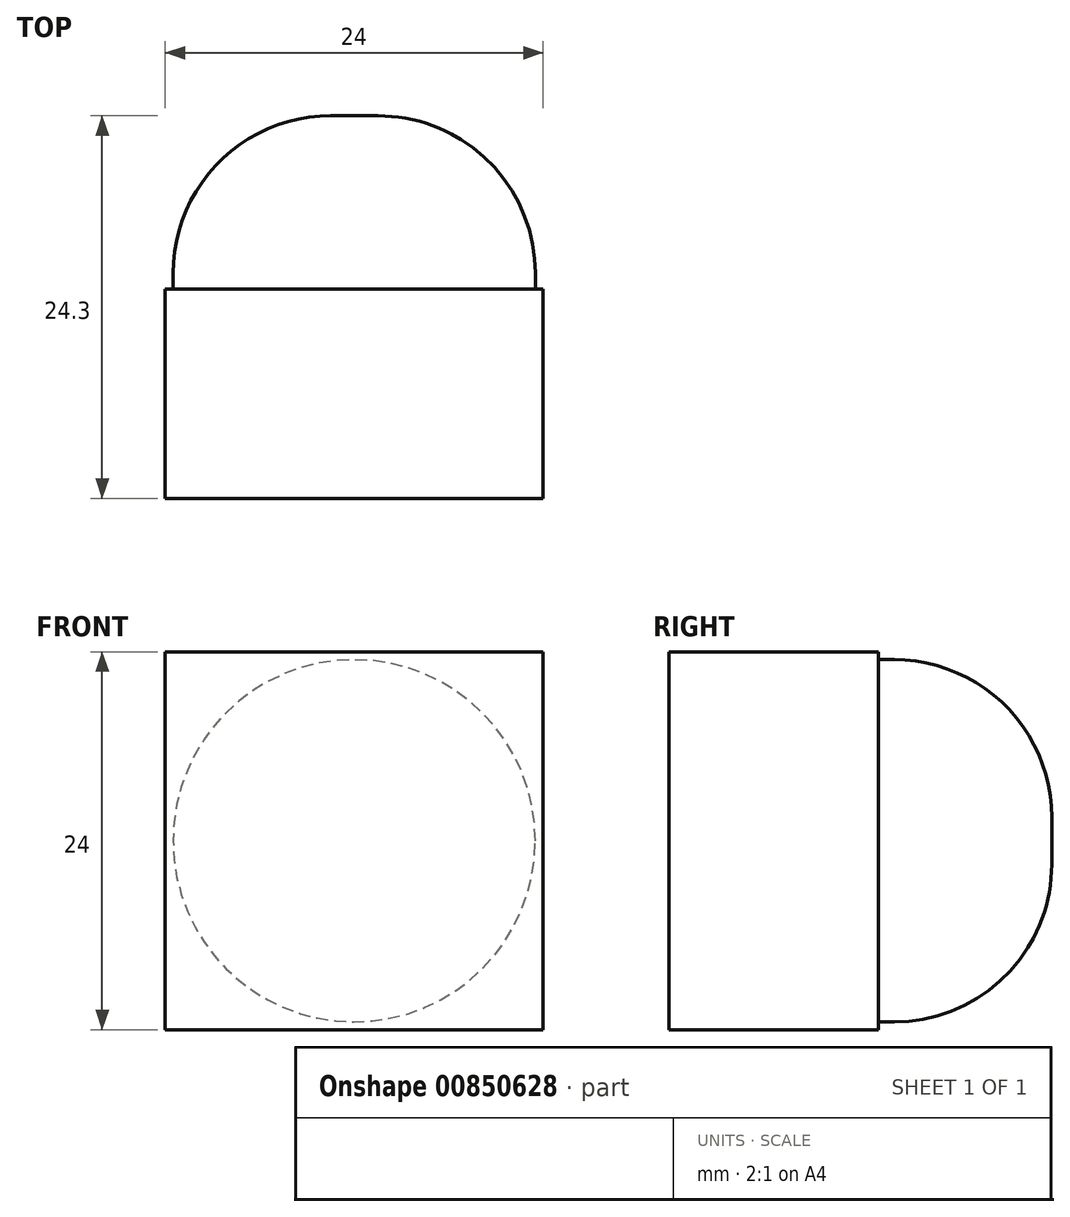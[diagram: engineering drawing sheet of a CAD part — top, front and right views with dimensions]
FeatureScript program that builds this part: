
annotation { "Feature Type Name" : "Feature", "Feature Type Description" : "" }
export const myFeature = defineFeature(function(context is Context, id is Id, definition is map)
    precondition{}
    {
        {
            var Q0;
            Q0=qCreatedBy(makeId("Front.planeOp"),FACE);
            var sketch = newSketch(context, id + "F0", { "sketchPlane" : qUnion([Q0])});
            skLineSegment(sketch, "E0.bottom", {"start": v(16.5, -12.5) * mm, "end": v(-16.5, -12.5) * mm});
            skLineSegment(sketch, "E0.top", {"start": v(16.5, 12.5) * mm, "end": v(-16.5, 12.5) * mm});
            skLineSegment(sketch, "E0.left", {"start": v(16.5, -12.5) * mm, "end": v(16.5, 12.5) * mm});
            skLineSegment(sketch, "E0.right", {"start": v(-16.5, -12.5) * mm, "end": v(-16.5, 12.5) * mm});
            skPoint(sketch, "E0.middle", {"position": v(0, 0) * mm});
            skLineSegment(sketch, "E1.bottom", {"start": v(-12, -12) * mm, "end": v(12, -12) * mm});
            skLineSegment(sketch, "E1.top", {"start": v(-12, 12) * mm, "end": v(12, 12) * mm});
            skLineSegment(sketch, "E1.left", {"start": v(-12, -12) * mm, "end": v(-12, 12) * mm});
            skLineSegment(sketch, "E1.right", {"start": v(12, -12) * mm, "end": v(12, 12) * mm});
            skLineSegment(sketch, "E2", {"start": v(16.5, 12.5) * mm, "end": v(14.2, 12.5) * mm});
            skLineSegment(sketch, "E3", {"start": v(14.2, 12.5) * mm, "end": v(14.2, 0) * mm});
            skCircle(sketch, "E4", {"center": v(14.2, 0) * mm, "radius": 0.75 * mm});
            skLineSegment(sketch, "E5.MirrorCS", {"start": v(-14.2, 12.5) * mm, "end": v(-14.2, 0) * mm});
            skCircle(sketch, "E6.MirrorC", {"center": v(-14.2, 0) * mm, "radius": 0.75 * mm});
            skSolve(sketch);
        }
        {
            var Q0;
            Q0 = qSketchRegion(id + "F0", true);
            var Q1;
            Q1=makeQuery(id+"F0.imprint","IMPRINT",FACE,{"disambiguationData":[TD([[makeQuery(id+"F0.imprint","IMPRINT",EDGE,{"derivedFrom":sQuery(id+"F0.wireOp",EDGE,"E1.bottom")}),1.0]])]});
            extrude(context, id + "F1", {"entities" : qUnion([Q0, Q1]), "depth" : 10 * mm, "offsetDistance" : 25 * mm});
        }
        {
            var Q0;
            Q0=makeQuery(id+"F0.imprint","IMPRINT",FACE,{"disambiguationData":[TD([[makeQuery(id+"F0.imprint","IMPRINT",EDGE,{"derivedFrom":sQuery(id+"F0.wireOp",EDGE,"E1.bottom")}),1.0]])]});
            extrude(context, id + "F2", {"entities" : qUnion([Q0]), "operationType" : NewBodyOperationType.ADD, "oppositeDirection" : true, "depth" : 3.3 * mm, "offsetDistance" : 25 * mm});
        }
        {
            var Q0;
            Q0=makeQuery(id+"F2.opExtrude","CAP_FACE",FACE,{"disambiguationData":[OSD([sQuery(id+"F0.wireOp",EDGE,"E1.bottom"),sQuery(id+"F0.wireOp",EDGE,"E1.top"),sQuery(id+"F0.wireOp",EDGE,"E1.left"),sQuery(id+"F0.wireOp",EDGE,"E1.right")])],"isStart":false});
            var sketch = newSketch(context, id + "F3", { "sketchPlane" : qUnion([Q0])});
            skCircle(sketch, "E7", {"center": v(0, 0) * mm, "radius": 11.5 * mm});
            skSolve(sketch);
        }
        {
            var Q0;
            Q0=makeQuery(id+"F3.imprint","IMPRINT",FACE,{"disambiguationData":[TD([[makeQuery(id+"F3.imprint","IMPRINT",EDGE,{"derivedFrom":sQuery(id+"F3.wireOp",EDGE,"E7")}),1.0]])]});
            extrude(context, id + "F4", {"entities" : qUnion([Q0]), "operationType" : NewBodyOperationType.ADD, "depth" : 11 * mm, "offsetDistance" : 25 * mm});
        }
        {
            var Q0;
            Q0=makeQuery(id+"F4.opExtrude","CAP_FACE",FACE,{"disambiguationData":[OSD([sQuery(id+"F3.wireOp",EDGE,"E7")])],"isStart":false});
            fillet(context, id + "F5", {"entities" : qUnion([Q0]), "radius" : 10 * mm, "tangentPropagation" : true, "allowEdgeOverflow" : false});
        }
        {
            var Q0;
            Q0=makeQuery(id+"F0.imprint","IMPRINT",FACE,{"disambiguationData":[TD([[makeQuery(id+"F0.imprint","IMPRINT",EDGE,{"derivedFrom":sQuery(id+"F0.wireOp",EDGE,"E4")}),1.0]])]});
            var Q1;
            Q1=makeQuery(id+"F0.imprint","IMPRINT",FACE,{"disambiguationData":[TD([[makeQuery(id+"F0.imprint","IMPRINT",EDGE,{"derivedFrom":sQuery(id+"F0.wireOp",EDGE,"E6.MirrorC")}),-1.0]])]});
            extrude(context, id + "F6", {"entities" : qUnion([Q0, Q1]), "operationType" : NewBodyOperationType.REMOVE, "depth" : 10 * mm, "offsetDistance" : 25 * mm});
        }
    });
